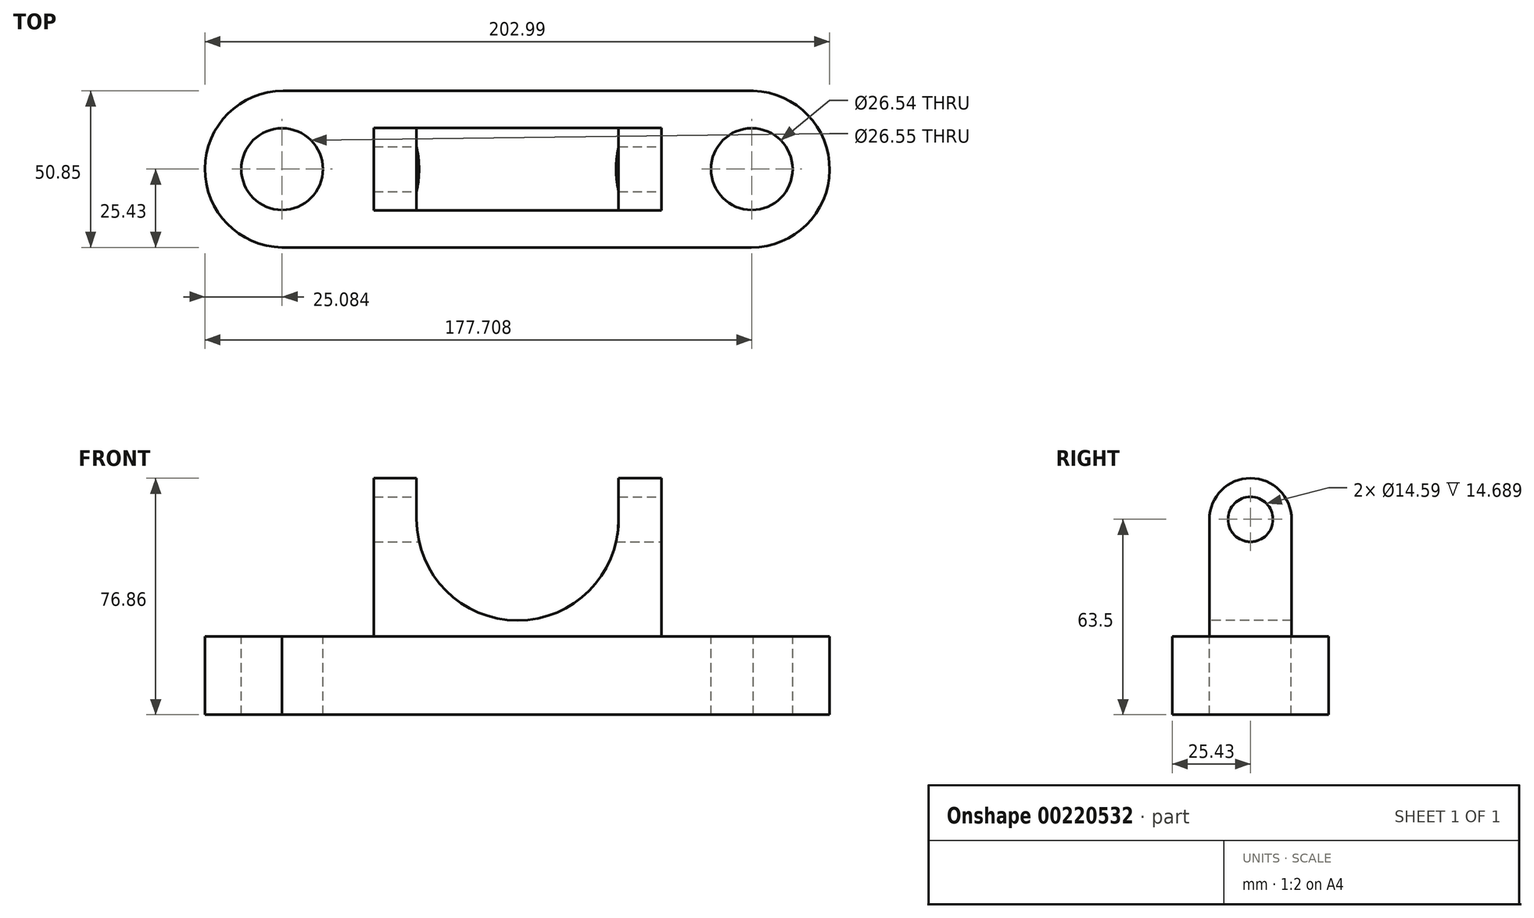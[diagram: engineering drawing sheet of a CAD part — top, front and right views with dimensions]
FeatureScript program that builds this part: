
annotation { "Feature Type Name" : "Feature", "Feature Type Description" : "" }
export const myFeature = defineFeature(function(context is Context, id is Id, definition is map)
    precondition{}
    {
        {
            var Q0;
            Q0=qCreatedBy(makeId("Top.planeOp"),FACE);
            var sketch = newSketch(context, id + "F0", { "sketchPlane" : qUnion([Q0])});
            skCircle(sketch, "E0", {"center": v(-76.18, 0) * mm, "radius": 25.42 * mm});
            skLineSegment(sketch, "E1", {"start": v(-76.18, 25.42) * mm, "end": v(76.66, 25.42) * mm});
            skCircle(sketch, "E2", {"center": v(75.96, 0) * mm, "radius": 25.43 * mm});
            skLineSegment(sketch, "E3", {"start": v(-76.52, -25.42) * mm, "end": v(75.96, -25.43) * mm});
            skSolve(sketch);
        }
        {
            var Q0;
            {var subQ0=sQuery(id+"F0.wireOp",EDGE,"E1");var subQ1=sQuery(id+"F0.wireOp",EDGE,"E0");var subQ2=makeQuery(id+"F0.imprint","INTERSECT",VERTEX,{"derivedFrom":[subQ1,subQ0]});Q0=makeQuery(id+"F0.imprint","IMPRINT",FACE,{"disambiguationData":[TD([[makeQuery(id+"F0.imprint","IMPRINT",EDGE,{"disambiguationData":[TD([[subQ2,1.0]])],"derivedFrom":subQ1}),-1.0]])]});}
            var Q1;
            {var subQ0=sQuery(id+"F0.wireOp",EDGE,"E0");var subQ1=makeQuery(id+"F0.imprint","INTERSECT",VERTEX,{"derivedFrom":[subQ0,sQuery(id+"F0.wireOp",EDGE,"E1")]});Q1=makeQuery(id+"F0.imprint","IMPRINT",FACE,{"disambiguationData":[TD([[makeQuery(id+"F0.imprint","IMPRINT",EDGE,{"disambiguationData":[TD([[subQ1,-1.0]])],"derivedFrom":subQ0}),1.0]])]});}
            var Q2;
            {var subQ0=sQuery(id+"F0.wireOp",EDGE,"E2");var subQ1=sQuery(id+"F0.wireOp",EDGE,"E1");var subQ2=makeQuery(id+"F0.imprint","INTERSECT",VERTEX,{"disambiguationData":[OD(0.0)],"derivedFrom":[subQ1,subQ0]});Q2=makeQuery(id+"F0.imprint","IMPRINT",FACE,{"disambiguationData":[TD([[makeQuery(id+"F0.imprint","IMPRINT",EDGE,{"disambiguationData":[TD([[subQ2,1.0]])],"derivedFrom":subQ1}),-1.0]])]});}
            extrude(context, id + "F1", {"entities" : qUnion([Q0, Q1, Q2]), "oppositeDirection" : true, "depth" : 25.4 * mm});
        }
        {
            var Q0;
            Q0=makeQuery(id+"F1.opExtrude","CAP_FACE",FACE,{"disambiguationData":[OSD([sQuery(id+"F0.wireOp",EDGE,"E0"),sQuery(id+"F0.wireOp",EDGE,"E1"),sQuery(id+"F0.wireOp",EDGE,"E2"),sQuery(id+"F0.wireOp",EDGE,"E3")])],"isStart":true});
            var sketch = newSketch(context, id + "F2", { "sketchPlane" : qUnion([Q0])});
            skCircle(sketch, "E4", {"center": v(-76.52, 0) * mm, "radius": 13.28 * mm});
            skCircle(sketch, "E5", {"center": v(76.1, 0) * mm, "radius": 13.27 * mm});
            skSolve(sketch);
        }
        {
            var Q0;
            Q0=makeQuery(id+"F2.imprint","IMPRINT",FACE,{"disambiguationData":[TD([[makeQuery(id+"F2.imprint","IMPRINT",EDGE,{"derivedFrom":sQuery(id+"F2.wireOp",EDGE,"E4")}),1.0]])]});
            var Q1;
            Q1=makeQuery(id+"F2.imprint","IMPRINT",FACE,{"disambiguationData":[TD([[makeQuery(id+"F2.imprint","IMPRINT",EDGE,{"derivedFrom":sQuery(id+"F2.wireOp",EDGE,"E5")}),1.0]])]});
            extrude(context, id + "F3", {"entities" : qUnion([Q0, Q1]), "operationType" : NewBodyOperationType.REMOVE, "endBound" : BoundingType.THROUGH_ALL, "oppositeDirection" : true, "depth" : 25.4 * mm});
        }
        {
            var Q0;
            Q0=makeQuery(id+"F1.opExtrude","CAP_FACE",FACE,{"disambiguationData":[OSD([sQuery(id+"F0.wireOp",EDGE,"E0"),sQuery(id+"F0.wireOp",EDGE,"E1"),sQuery(id+"F0.wireOp",EDGE,"E2"),sQuery(id+"F0.wireOp",EDGE,"E3")])],"isStart":true});
            var sketch = newSketch(context, id + "F4", { "sketchPlane" : qUnion([Q0])});
            skLineSegment(sketch, "E6.bottom", {"start": v(46.7, 13.36) * mm, "end": v(-46.7, 13.36) * mm});
            skLineSegment(sketch, "E6.top", {"start": v(46.7, -13.36) * mm, "end": v(-46.7, -13.36) * mm});
            skLineSegment(sketch, "E6.left", {"start": v(46.7, 13.36) * mm, "end": v(46.7, -13.36) * mm});
            skLineSegment(sketch, "E6.right", {"start": v(-46.7, 13.36) * mm, "end": v(-46.7, -13.36) * mm});
            skPoint(sketch, "E6.middle", {"position": v(0, 0) * mm});
            skSolve(sketch);
        }
        {
            var Q0;
            Q0=makeQuery(id+"F4.imprint","IMPRINT",FACE,{"disambiguationData":[TD([[makeQuery(id+"F4.imprint","IMPRINT",EDGE,{"derivedFrom":sQuery(id+"F4.wireOp",EDGE,"E6.bottom")}),1.0]])]});
            extrude(context, id + "F5", {"entities" : qUnion([Q0]), "operationType" : NewBodyOperationType.ADD, "depth" : 38.1 * mm});
        }
        {
            var Q0;
            Q0=makeQuery(id+"F5.opExtrude","SWEPT_FACE",FACE,{"disambiguationData":[OSD([sQuery(id+"F4.wireOp",EDGE,"E6.top")])]});
            var sketch = newSketch(context, id + "F6", { "sketchPlane" : qUnion([Q0])});
            skCircle(sketch, "E7", {"center": v(0, 38.1) * mm, "radius": 32.83 * mm});
            skSolve(sketch);
        }
        {
            var Q0;
            {var subQ0=sQuery(id+"F6.wireOp",EDGE,"E7");var subQ1=makeQuery(id+"F5.opExtrude","CAP_EDGE",EDGE,{"disambiguationData":[OSD([sQuery(id+"F4.wireOp",EDGE,"E6.top")])],"isStart":false});var subQ2=makeQuery(id+"F6.imprint","INTERSECT",VERTEX,{"disambiguationData":[OD(0.0)],"derivedFrom":[subQ1,subQ0]});Q0=makeQuery(id+"F6.imprint","IMPRINT",FACE,{"disambiguationData":[TD([[makeQuery(id+"F6.imprint","IMPRINT",EDGE,{"disambiguationData":[TD([[subQ2,1.0]])],"derivedFrom":subQ0}),1.0]])]});}
            var Q1;
            {var subQ0=sQuery(id+"F6.wireOp",EDGE,"E7");var subQ1=makeQuery(id+"F5.opExtrude","CAP_EDGE",EDGE,{"disambiguationData":[OSD([sQuery(id+"F4.wireOp",EDGE,"E6.top")])],"isStart":false});var subQ2=makeQuery(id+"F6.imprint","INTERSECT",VERTEX,{"disambiguationData":[OD(0.0)],"derivedFrom":[subQ1,subQ0]});Q1=makeQuery(id+"F6.imprint","IMPRINT",FACE,{"disambiguationData":[TD([[makeQuery(id+"F6.imprint","IMPRINT",EDGE,{"disambiguationData":[TD([[subQ2,-1.0]])],"derivedFrom":subQ0}),1.0]])]});}
            extrude(context, id + "F7", {"entities" : qUnion([Q0, Q1]), "operationType" : NewBodyOperationType.REMOVE, "endBound" : BoundingType.THROUGH_ALL, "oppositeDirection" : true, "depth" : 25.4 * mm});
        }
        {
            var Q0;
            {var subQ0=sQuery(id+"F4.wireOp",EDGE,"E6.bottom");var subQ1=sQuery(id+"F4.wireOp",EDGE,"E6.left");var subQ2=sQuery(id+"F4.wireOp",EDGE,"E6.top");Q0=makeQuery(id+"F7.boolean.opBoolean","SPLIT",FACE,{"disambiguationData":[TD([makeQuery(id+"F5.opExtrude","SWEPT_FACE",FACE,{"disambiguationData":[OSD([subQ1])]})])],"derivedFrom":makeQuery(id+"F5.opExtrude","CAP_FACE",FACE,{"disambiguationData":[OSD([subQ0,subQ2,subQ1,sQuery(id+"F4.wireOp",EDGE,"E6.right")])],"isStart":false})});}
            var sketch = newSketch(context, id + "F8", { "sketchPlane" : qUnion([Q0])});
            skLineSegment(sketch, "E8.bottom", {"start": v(46.7, 0) * mm, "end": v(32.83, 0) * mm});
            skLineSegment(sketch, "E8.top", {"start": v(46.7, 13.36) * mm, "end": v(32.83, 13.36) * mm});
            skLineSegment(sketch, "E8.left", {"start": v(46.7, 0) * mm, "end": v(46.7, 13.36) * mm});
            skLineSegment(sketch, "E8.right", {"start": v(32.83, 0) * mm, "end": v(32.83, 13.36) * mm});
            skSolve(sketch);
        }
        {
            var Q0;
            Q0=makeQuery(id+"F8.imprint","IMPRINT",FACE,{"disambiguationData":[TD([[makeQuery(id+"F8.imprint","IMPRINT",EDGE,{"derivedFrom":sQuery(id+"F8.wireOp",EDGE,"E8.bottom")}),-1.0]])]});
            var Q1;
            Q1=sQuery(id+"F8.wireOp",EDGE,"E8.bottom");
            revolve(context, id + "F9", {"operationType" : NewBodyOperationType.ADD, "entities" : qUnion([Q0]), "axis" : qUnion([Q1]), "revolveType" : RevolveType.FULL});
        }
        {
            var Q0;
            {var subQ0=sQuery(id+"F4.wireOp",EDGE,"E6.bottom");var subQ1=sQuery(id+"F4.wireOp",EDGE,"E6.right");var subQ2=sQuery(id+"F4.wireOp",EDGE,"E6.top");Q0=makeQuery(id+"F7.boolean.opBoolean","SPLIT",FACE,{"disambiguationData":[TD([makeQuery(id+"F5.opExtrude","SWEPT_FACE",FACE,{"disambiguationData":[OSD([subQ1])]})])],"derivedFrom":makeQuery(id+"F5.opExtrude","CAP_FACE",FACE,{"disambiguationData":[OSD([subQ0,subQ2,sQuery(id+"F4.wireOp",EDGE,"E6.left"),subQ1])],"isStart":false})});}
            var sketch = newSketch(context, id + "F10", { "sketchPlane" : qUnion([Q0])});
            skLineSegment(sketch, "E9.bottom", {"start": v(-32.83, 0) * mm, "end": v(-46.7, 0) * mm});
            skLineSegment(sketch, "E9.top", {"start": v(-32.83, 13.36) * mm, "end": v(-46.7, 13.36) * mm});
            skLineSegment(sketch, "E9.left", {"start": v(-32.83, 0) * mm, "end": v(-32.83, 13.36) * mm});
            skLineSegment(sketch, "E9.right", {"start": v(-46.7, 0) * mm, "end": v(-46.7, 13.36) * mm});
            skSolve(sketch);
        }
        {
            var Q0;
            Q0=makeQuery(id+"F10.imprint","IMPRINT",FACE,{"disambiguationData":[TD([[makeQuery(id+"F10.imprint","IMPRINT",EDGE,{"derivedFrom":sQuery(id+"F10.wireOp",EDGE,"E9.bottom")}),-1.0]])]});
            var Q1;
            Q1=sQuery(id+"F10.wireOp",EDGE,"E9.bottom");
            revolve(context, id + "F11", {"operationType" : NewBodyOperationType.ADD, "entities" : qUnion([Q0]), "axis" : qUnion([Q1]), "revolveType" : RevolveType.FULL});
        }
        {
            var Q0;
            Q0=makeQuery(id+"F9.boolean.opBoolean","MERGE",FACE,{"derivedFrom":[makeQuery(id+"F5.opExtrude","SWEPT_FACE",FACE,{"disambiguationData":[OSD([sQuery(id+"F4.wireOp",EDGE,"E6.left")])]}),makeQuery(id+"F9.opRevolve","SWEPT_FACE",FACE,{"disambiguationData":[OSD([sQuery(id+"F8.wireOp",EDGE,"E8.left")])]})]});
            var sketch = newSketch(context, id + "F12", { "sketchPlane" : qUnion([Q0])});
            skCircle(sketch, "E10", {"center": v(0, 38.1) * mm, "radius": 7.3 * mm});
            skSolve(sketch);
        }
        {
            var Q0;
            Q0=makeQuery(id+"F12.imprint","IMPRINT",FACE,{"disambiguationData":[TD([[makeQuery(id+"F12.imprint","IMPRINT",EDGE,{"derivedFrom":sQuery(id+"F12.wireOp",EDGE,"E10")}),1.0]])]});
            extrude(context, id + "F13", {"entities" : qUnion([Q0]), "operationType" : NewBodyOperationType.REMOVE, "endBound" : BoundingType.THROUGH_ALL, "oppositeDirection" : true, "depth" : 254 * mm});
        }
    });
